# Revit family: Toilet-Floor_Mount-KOHLER-Eir_Comfort_Height-K-77795_12
name_source: partatom
category: Plumbing Fixtures
revit_build: Autodesk Revit 2017 (Build: 20160225_1515(x64)
units: mm (PartAtom-declared; Revit-internal decimal feet)

## family parameters
Cut with Voids When Loaded = No
Host = Face
OmniClass Number = 23.31.19.00
OmniClass Title = Toilets
Part Type = Normal
Room Calculation Point = No
Round Connector Dimension = Use Diameter
Shared = No

## types (3) — shared parameters
ADA Compliant = Yes
Apparent Load = 1800 VA
Assembly Code = D2010100
CW Connection = Yes
Cold Water Inlet = Cold Water Inlet
Date Modified = 09/25/2020
Default Elevation = 0"
Description = One-piece elongated dual-flush intelligent chair-height toilet
Electrical Connector = Yes
Electrical Note = One dedicated circuit required, protected with Class A Ground-Fault Circuit-Interrupter (GFCI). Outside North America, this device may be known as a Residual Current Device (RCD)
Finish = Kohler-Vitreous_China-0-White
Flow Rate = 0 GPM
Flush Rate- GPF = 1.0 GPF
Flush Rate- LPF = 3.8 LPF
HW Connection = No
Height = 20 9/16"
Hot Water Inlet = Hot Water Inlet
Length = 27 9/16"
Manufacturer = KOHLER Co.
Master Format 2014 = 22 41 13.13
Master Format 2014 Name = Residential Water Closets
Material = Vitreous China
Pressure = 80.00 psi
Product Documentation Link = https://www.us.kohler.com
Product Name = Eir Comfort Height
Product Page URL = http://www.us.kohler.com
Rough-In = 12"
Seat Included = Yes
URL = https://www.us.kohler.com
Vent Connection = No
Voltage = 120 V
Waste Connection = Yes
Waste Water Outlet = Waste Water Outlet
WaterSense Certified = Yes
Width = 16 7/16"

## per-type parameters (varying)
| type | Model | Seat Finish | Type |
| 0-White | K-77795-0 | Kohler-Metal-0-White | 1 |
| 0SG-White With Sunrise Gold | K-77795-0SG | Kohler-Metal-PGD-Modern_Polished_Gold | 2 |
| 0RG-White With Rose Gold | K-77795-0RG | Kohler-Metal-RGD-Polished_Rose_Gold | 3 |

## geometry (parser evidence)
native form markers: Sweep x4
no freeform markers — native parametric forms only
